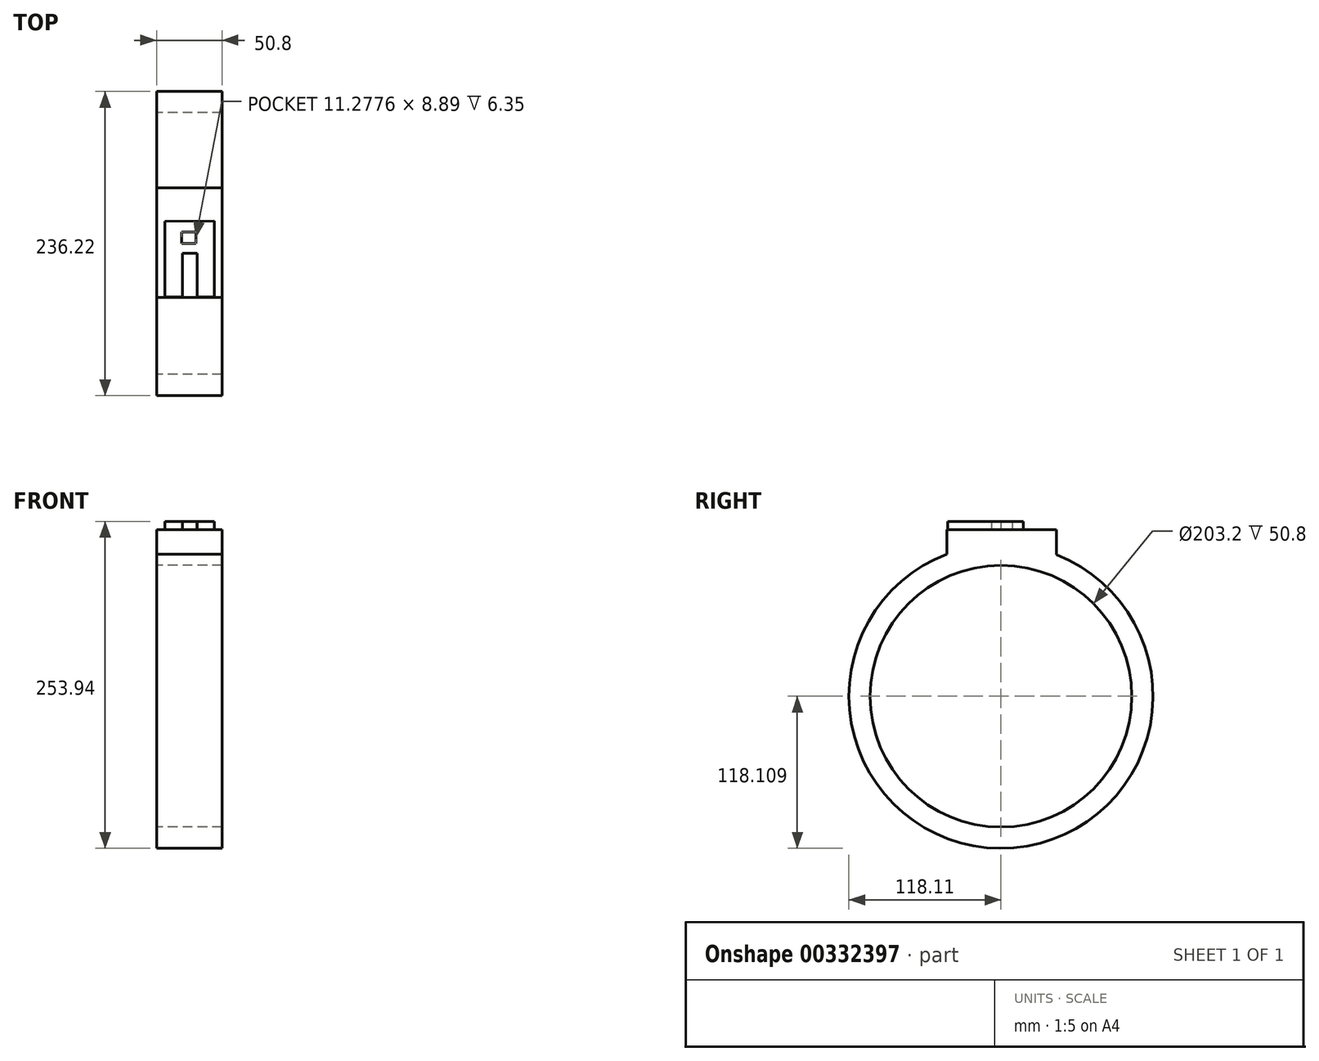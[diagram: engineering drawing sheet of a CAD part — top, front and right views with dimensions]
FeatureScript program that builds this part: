
annotation { "Feature Type Name" : "Feature", "Feature Type Description" : "" }
export const myFeature = defineFeature(function(context is Context, id is Id, definition is map)
    precondition{}
    {
        {
            var Q0;
            Q0=qCreatedBy(makeId("Front.planeOp"),FACE);
            var sketch = newSketch(context, id + "F0", { "sketchPlane" : qUnion([Q0])});
            skLineSegment(sketch, "E0.bottom", {"start": v(-83.3, 79.67) * mm, "end": v(-32.5, 79.67) * mm});
            skLineSegment(sketch, "E0.top", {"start": v(-83.3, 63.16) * mm, "end": v(-32.5, 63.16) * mm});
            skLineSegment(sketch, "E0.left", {"start": v(-83.3, 79.67) * mm, "end": v(-83.3, 63.16) * mm});
            skLineSegment(sketch, "E0.right", {"start": v(-32.5, 79.67) * mm, "end": v(-32.5, 63.16) * mm});
            skLineSegment(sketch, "E1", {"start": v(-257.84, -38.44) * mm, "end": v(137.82, -38.44) * mm});
            skSolve(sketch);
        }
        {
            var Q0;
            Q0=makeQuery(id+"F0.imprint","IMPRINT",FACE,{"disambiguationData":[TD([[makeQuery(id+"F0.imprint","IMPRINT",EDGE,{"derivedFrom":sQuery(id+"F0.wireOp",EDGE,"E0.bottom")}),-1.0]])]});
            var Q1;
            Q1=sQuery(id+"F0.wireOp",EDGE,"E1");
            revolve(context, id + "F1", {"entities" : qUnion([Q0]), "axis" : qUnion([Q1]), "revolveType" : RevolveType.FULL});
        }
        {
            var Q0;
            Q0=makeQuery(id+"F1.opRevolve","SWEPT_FACE",FACE,{"disambiguationData":[OSD([sQuery(id+"F0.wireOp",EDGE,"E0.right")])]});
            var sketch = newSketch(context, id + "F2", { "sketchPlane" : qUnion([Q0])});
            skLineSegment(sketch, "E2", {"start": v(43.2, 71.48) * mm, "end": v(43.2, 91.04) * mm});
            skLineSegment(sketch, "E3", {"start": v(43.2, 91.04) * mm, "end": v(-41.89, 91.04) * mm});
            skLineSegment(sketch, "E4", {"start": v(-41.89, 91.04) * mm, "end": v(-41.89, 72) * mm});
            skSolve(sketch);
        }
        {
            var Q0;
            Q0 = qSketchRegion(id + "F2", true);
            var Q1;
            {var subQ0=sQuery(id+"F2.wireOp",EDGE,"E2");Q1=makeQuery(id+"F2.imprint","IMPRINT",FACE,{"disambiguationData":[TD([[makeQuery(id+"F2.imprint","IMPRINT",EDGE,{"derivedFrom":subQ0}),1.0]])]});}
            extrude(context, id + "F3", {"entities" : qUnion([Q0, Q1]), "operationType" : NewBodyOperationType.ADD, "oppositeDirection" : true, "depth" : 50.8 * mm});
        }
        {
            var Q0;
            Q0=makeQuery(id+"F3.opExtrude","SWEPT_FACE",FACE,{"disambiguationData":[OSD([sQuery(id+"F2.wireOp",EDGE,"E3")])]});
            var sketch = newSketch(context, id + "F4", { "sketchPlane" : qUnion([Q0])});
            skLineSegment(sketch, "E5", {"start": v(-76.26, -41.07) * mm, "end": v(-63.56, -41.07) * mm});
            skLineSegment(sketch, "E6", {"start": v(-63.56, -41.07) * mm, "end": v(-63.56, -7.77) * mm});
            skLineSegment(sketch, "E7", {"start": v(-63.56, -7.77) * mm, "end": v(-51.54, -7.77) * mm});
            skLineSegment(sketch, "E8", {"start": v(-51.54, -7.77) * mm, "end": v(-51.54, -41.76) * mm});
            skLineSegment(sketch, "E9", {"start": v(-51.54, -41.76) * mm, "end": v(-38.84, -41.76) * mm});
            skLineSegment(sketch, "E10", {"start": v(-38.84, -41.76) * mm, "end": v(-38.84, 17.28) * mm});
            skLineSegment(sketch, "E11", {"start": v(-38.84, 17.28) * mm, "end": v(-76.94, 17.28) * mm});
            skLineSegment(sketch, "E12", {"start": v(-76.94, 17.28) * mm, "end": v(-76.94, -41.07) * mm});
            skLineSegment(sketch, "E13", {"start": v(-64, 8.89) * mm, "end": v(-64, 0) * mm});
            skLineSegment(sketch, "E14", {"start": v(-64, 0) * mm, "end": v(-52.72, 0) * mm});
            skLineSegment(sketch, "E15", {"start": v(-52.72, 0) * mm, "end": v(-52.72, 8.89) * mm});
            skLineSegment(sketch, "E16", {"start": v(-52.72, 8.89) * mm, "end": v(-64, 8.89) * mm});
            skSolve(sketch);
        }
        {
            var Q0;
            Q0=makeQuery(id+"F4.imprint","IMPRINT",FACE,{"disambiguationData":[TD([[makeQuery(id+"F4.imprint","IMPRINT",EDGE,{"derivedFrom":sQuery(id+"F4.wireOp",EDGE,"E13")}),-1.0]])]});
            var sketch = newSketch(context, id + "F5", { "sketchPlane" : qUnion([Q0])});
            skLineSegment(sketch, "E17", {"start": v(-76.91, 17.38) * mm, "end": v(-76.91, -41.45) * mm});
            skLineSegment(sketch, "E18", {"start": v(-76.91, -41.45) * mm, "end": v(-63.37, -41.45) * mm});
            skLineSegment(sketch, "E19", {"start": v(-63.37, -41.45) * mm, "end": v(-63.37, -7.56) * mm});
            skLineSegment(sketch, "E20", {"start": v(-63.37, -7.56) * mm, "end": v(-51.72, -7.56) * mm});
            skLineSegment(sketch, "E21", {"start": v(-51.72, -7.56) * mm, "end": v(-51.72, -41.45) * mm});
            skLineSegment(sketch, "E22", {"start": v(-51.72, -41.45) * mm, "end": v(-38.33, -41.45) * mm});
            skLineSegment(sketch, "E23", {"start": v(-38.33, -41.45) * mm, "end": v(-38.33, 17.49) * mm});
            skLineSegment(sketch, "E24", {"start": v(-38.33, 17.49) * mm, "end": v(-76.91, 17.38) * mm});
            skSolve(sketch);
        }
        {
            var Q0;
            Q0 = qSketchRegion(id + "F5", true);
            extrude(context, id + "F6", {"entities" : qUnion([Q0]), "operationType" : NewBodyOperationType.ADD, "depth" : 6.35 * mm});
        }
        {
            var Q0;
            Q0 = qSketchRegion(id + "F4", true);
            extrude(context, id + "F7", {"entities" : qUnion([Q0]), "operationType" : NewBodyOperationType.REMOVE, "depth" : 6.35 * mm});
        }
    });
